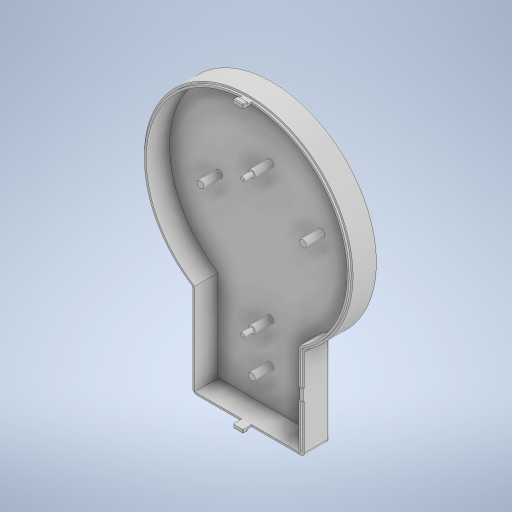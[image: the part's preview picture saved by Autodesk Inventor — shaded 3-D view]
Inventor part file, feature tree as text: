
AUTODESK INVENTOR PART (.ipt)
format: ipt  version: 2024 (Build 280153000, 153)  size: 551,936 bytes
history: native  units: mm
features: extrude x14, sketch x14, fillet x7
ambient origin geometry x8: Origin, YZ Plane, XZ Plane, XY Plane, X Axis, Y Axis, Z Axis, Center Point
bodies: Body1 (feature_tree)
feature tree (35):
  extrude  "Extrusion2"  Depth=102.0mm
  sketch  "Esquisse2"
  extrude  "Extrusion5"  Depth=26.4mm
  sketch  "Esquisse4"
  sketch  "Esquisse5"
  extrude  "Extrusion6"  Depth=90.0mm
  extrude  "Extrusion7"  Depth=26.4mm
  extrude  "Extrusion8"  Depth=2.0mm TaperAngle=0.0deg
  extrude  "Extrusion10"  Depth=3.5mm
  fillet  "Congé2"  Radius=39.1mm
  fillet  "Congé3"  Radius=26.4mm
  extrude  "Extrusion11"  Depth=3.5mm
  extrude  "Extrusion12"  Depth=107.68mm
  extrude  "Extrusion13"  Depth=26.4mm
  fillet  "Congé4"  Radius=9.2mm
  fillet  "Congé6"  Radius=2.0mm
  extrude  "Extrusion14"  Depth=2.0mm
  extrude  "Extrusion17"  Depth=4.6mm TaperAngle=0.0deg
  fillet  "Congé7"  Radius=4.6mm
  extrude  "Extrusion18"  Depth=3.5mm
  fillet  "Congé8"  Radius=18.5mm
  extrude  "Extrusion19"  Depth=3.5mm
  extrude  "Extrusion20"  Depth=3.5mm
  fillet  "Congé9"  Radius=26.0mm
  sketch  "Esquisse1"
  sketch  "Esquisse6"
  sketch  "Esquisse7"
  sketch  "Esquisse8"
  sketch  "Esquisse9"
  sketch  "Esquisse10"
  sketch  "Esquisse11"
  sketch  "Esquisse17"
  sketch  "Esquisse18"
  sketch  "Esquisse19"
  sketch  "Esquisse20"
